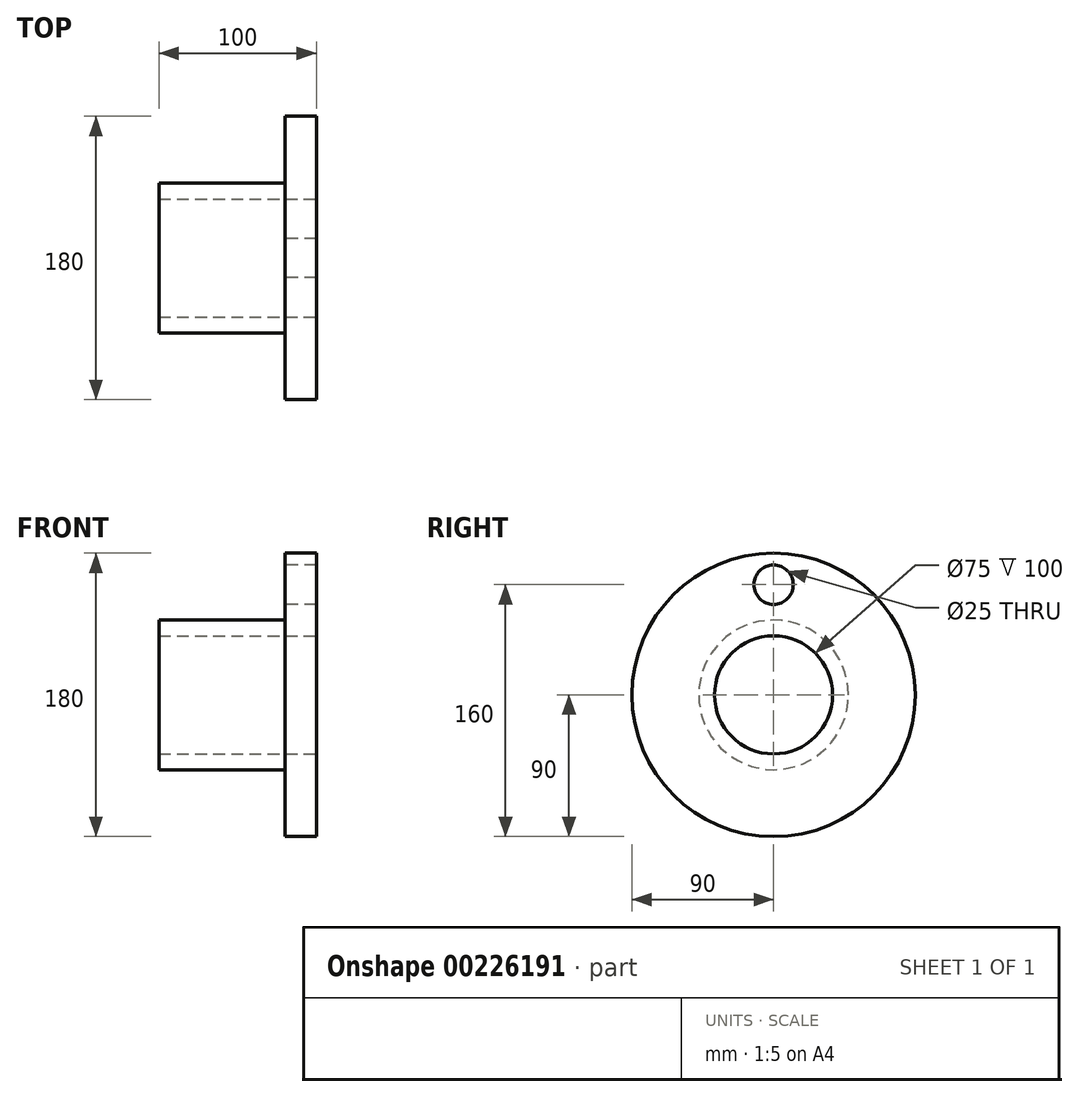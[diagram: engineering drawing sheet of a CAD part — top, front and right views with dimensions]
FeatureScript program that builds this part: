
annotation { "Feature Type Name" : "Feature", "Feature Type Description" : "" }
export const myFeature = defineFeature(function(context is Context, id is Id, definition is map)
    precondition{}
    {
        {
            var Q0;
            Q0=qCreatedBy(makeId("Front.planeOp"),FACE);
            var sketch = newSketch(context, id + "F0", { "sketchPlane" : qUnion([Q0])});
            skLineSegment(sketch, "E0", {"start": v(0, 0) * mm, "end": v(-108.98, 0) * mm, "construction": true});
            skLineSegment(sketch, "E1.bottom", {"start": v(-100, 37.5) * mm, "end": v(0, 37.5) * mm});
            skLineSegment(sketch, "E1.top", {"start": v(-20, 90) * mm, "end": v(0, 90) * mm});
            skLineSegment(sketch, "E1.left", {"start": v(-100, 47.5) * mm, "end": v(-100, 37.5) * mm});
            skLineSegment(sketch, "E1.right", {"start": v(0, 90) * mm, "end": v(0, 37.5) * mm});
            skLineSegment(sketch, "E2.top", {"start": v(-100, 47.5) * mm, "end": v(-20, 47.5) * mm});
            skLineSegment(sketch, "E2.right", {"start": v(-20, 47.5) * mm, "end": v(-20, 90) * mm});
            skSolve(sketch);
        }
        {
            var Q0;
            Q0=makeQuery(id+"F0.imprint","IMPRINT",FACE,{"disambiguationData":[TD([[makeQuery(id+"F0.imprint","IMPRINT",EDGE,{"derivedFrom":sQuery(id+"F0.wireOp",EDGE,"E1.bottom")}),1.0]])]});
            var Q1;
            Q1=sQuery(id+"F0.wireOp",EDGE,"E0");
            revolve(context, id + "F1", {"entities" : qUnion([Q0]), "axis" : qUnion([Q1]), "revolveType" : RevolveType.FULL});
        }
        {
            var Q0;
            Q0=makeQuery(id+"F1.opRevolve","SWEPT_FACE",FACE,{"disambiguationData":[OSD([sQuery(id+"F0.wireOp",EDGE,"E2.right")])]});
            var sketch = newSketch(context, id + "F2", { "sketchPlane" : qUnion([Q0])});
            skCircle(sketch, "E3", {"center": v(0, 70) * mm, "radius": 12.5 * mm});
            skSolve(sketch);
        }
        {
            var Q0;
            Q0 = qSketchRegion(id + "F2", true);
            extrude(context, id + "F3", {"entities" : qUnion([Q0]), "operationType" : NewBodyOperationType.REMOVE, "oppositeDirection" : true, "depth" : 85 * mm});
        }
    });
